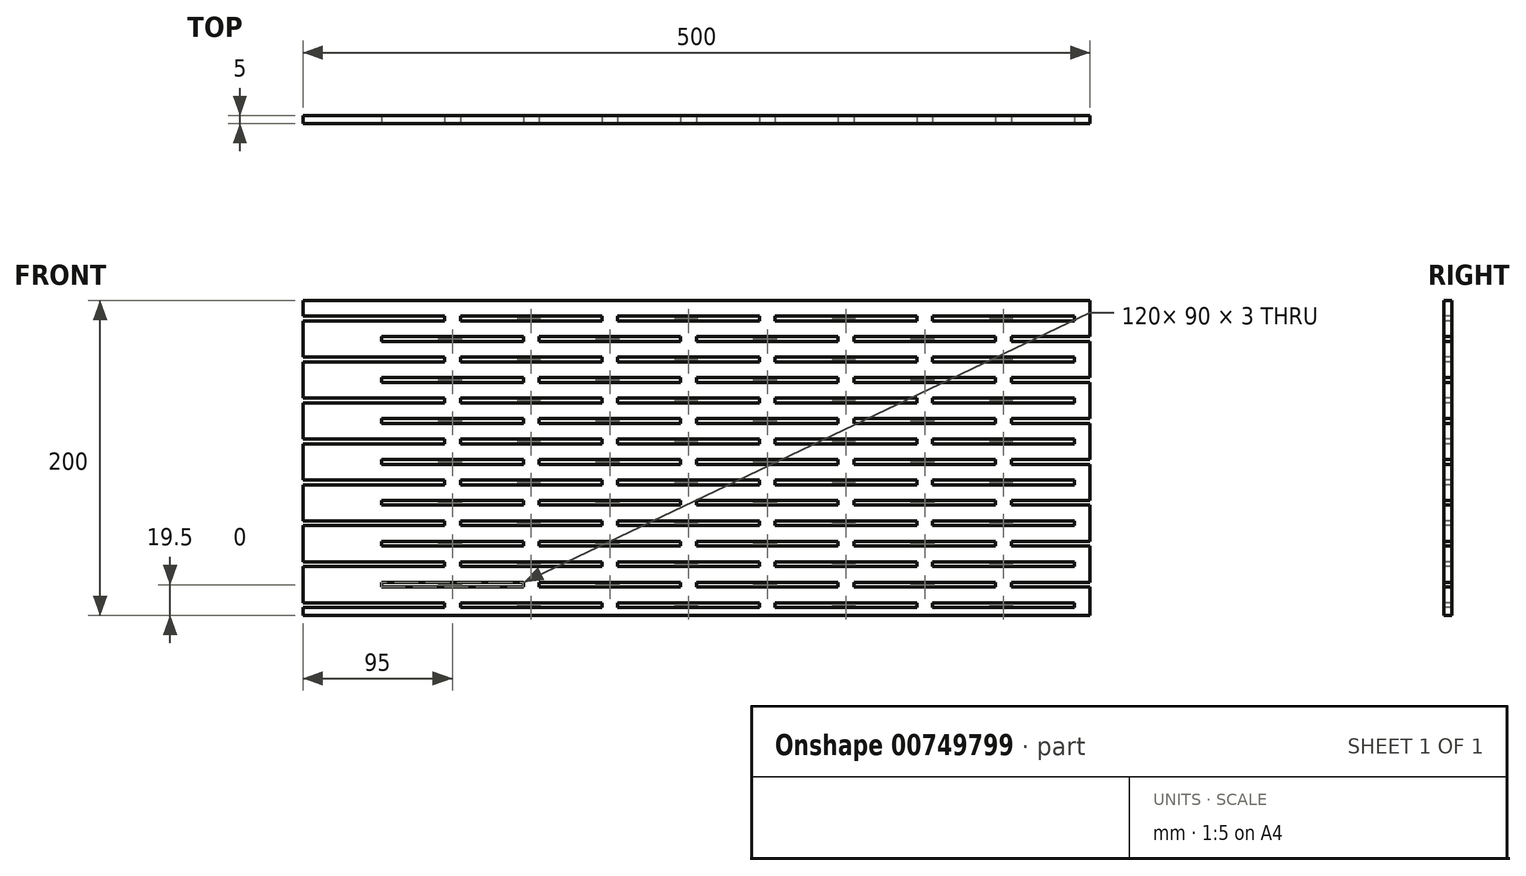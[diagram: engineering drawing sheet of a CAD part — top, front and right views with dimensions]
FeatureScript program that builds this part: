
annotation { "Feature Type Name" : "Feature", "Feature Type Description" : "" }
export const myFeature = defineFeature(function(context is Context, id is Id, definition is map)
    precondition{}
    {
        {
            var Q0;
            Q0=qCreatedBy(makeId("Front.planeOp"),FACE);
            var sketch = newSketch(context, id + "F0", { "sketchPlane" : qUnion([Q0])});
            skLineSegment(sketch, "E0.bottom", {"start": v(-250, 100) * mm, "end": v(250, 100) * mm});
            skLineSegment(sketch, "E0.top", {"start": v(-250, -100) * mm, "end": v(250, -100) * mm});
            skLineSegment(sketch, "E0.left", {"start": v(-250, 100) * mm, "end": v(-250, -100) * mm});
            skLineSegment(sketch, "E0.right", {"start": v(250, 100) * mm, "end": v(250, -100) * mm});
            skPoint(sketch, "E0.middle", {"position": v(0, 0) * mm});
            skSolve(sketch);
        }
        {
            var Q0;
            Q0=makeQuery(id+"F0.imprint","IMPRINT",FACE,{"disambiguationData":[TD([[makeQuery(id+"F0.imprint","IMPRINT",EDGE,{"derivedFrom":sQuery(id+"F0.wireOp",EDGE,"E0.bottom")}),-1.0]])]});
            extrude(context, id + "F1", {"entities" : qUnion([Q0]), "depth" : 5 * mm, "offsetDistance" : 25 * mm});
        }
        {
            var Q0;
            Q0=makeQuery(id+"F1.opExtrude","CAP_FACE",FACE,{"disambiguationData":[OSD([sQuery(id+"F0.wireOp",EDGE,"E0.bottom"),sQuery(id+"F0.wireOp",EDGE,"E0.top"),sQuery(id+"F0.wireOp",EDGE,"E0.left"),sQuery(id+"F0.wireOp",EDGE,"E0.right")])],"isStart":false});
            var sketch = newSketch(context, id + "F2", { "sketchPlane" : qUnion([Q0])});
            skLineSegment(sketch, "E1.bottom", {"start": v(-250, 90) * mm, "end": v(-160, 90) * mm});
            skLineSegment(sketch, "E1.top", {"start": v(-250, 87) * mm, "end": v(-160, 87) * mm});
            skLineSegment(sketch, "E1.left", {"start": v(-250, 90) * mm, "end": v(-250, 87) * mm});
            skLineSegment(sketch, "E1.right", {"start": v(-160, 90) * mm, "end": v(-160, 87) * mm});
            skLineSegment(sketch, "E2.bottom", {"start": v(-200, 77) * mm, "end": v(-110, 77) * mm});
            skLineSegment(sketch, "E2.top", {"start": v(-200, 74) * mm, "end": v(-110, 74) * mm});
            skLineSegment(sketch, "E2.left", {"start": v(-200, 77) * mm, "end": v(-200, 74) * mm});
            skLineSegment(sketch, "E2.right", {"start": v(-110, 77) * mm, "end": v(-110, 74) * mm});
            skLineSegment(sketch, "E3.0.1.0", {"start": v(-250, 64) * mm, "end": v(-160, 64) * mm});
            skLineSegment(sketch, "E3.0.1.1", {"start": v(-200, 51) * mm, "end": v(-110, 51) * mm});
            skLineSegment(sketch, "E3.0.1.2", {"start": v(-200, 48) * mm, "end": v(-110, 48) * mm});
            skLineSegment(sketch, "E3.0.1.3", {"start": v(-250, 61) * mm, "end": v(-160, 61) * mm});
            skLineSegment(sketch, "E3.0.1.4", {"start": v(-110, 51) * mm, "end": v(-110, 48) * mm});
            skLineSegment(sketch, "E3.0.1.5", {"start": v(-160, 64) * mm, "end": v(-160, 61) * mm});
            skLineSegment(sketch, "E3.0.1.6", {"start": v(-250, 64) * mm, "end": v(-250, 61) * mm});
            skLineSegment(sketch, "E3.0.1.7", {"start": v(-200, 51) * mm, "end": v(-200, 48) * mm});
            skLineSegment(sketch, "E3.0.2.0", {"start": v(-250, 38) * mm, "end": v(-160, 38) * mm});
            skLineSegment(sketch, "E3.0.2.1", {"start": v(-200, 25) * mm, "end": v(-110, 25) * mm});
            skLineSegment(sketch, "E3.0.2.2", {"start": v(-200, 22) * mm, "end": v(-110, 22) * mm});
            skLineSegment(sketch, "E3.0.2.3", {"start": v(-250, 35) * mm, "end": v(-160, 35) * mm});
            skLineSegment(sketch, "E3.0.2.4", {"start": v(-110, 25) * mm, "end": v(-110, 22) * mm});
            skLineSegment(sketch, "E3.0.2.5", {"start": v(-160, 38) * mm, "end": v(-160, 35) * mm});
            skLineSegment(sketch, "E3.0.2.6", {"start": v(-250, 38) * mm, "end": v(-250, 35) * mm});
            skLineSegment(sketch, "E3.0.2.7", {"start": v(-200, 25) * mm, "end": v(-200, 22) * mm});
            skLineSegment(sketch, "E3.0.3.0", {"start": v(-250, 12) * mm, "end": v(-160, 12) * mm});
            skLineSegment(sketch, "E3.0.3.1", {"start": v(-200, -1) * mm, "end": v(-110, -1) * mm});
            skLineSegment(sketch, "E3.0.3.2", {"start": v(-200, -4) * mm, "end": v(-110, -4) * mm});
            skLineSegment(sketch, "E3.0.3.3", {"start": v(-250, 9) * mm, "end": v(-160, 9) * mm});
            skLineSegment(sketch, "E3.0.3.4", {"start": v(-110, -1) * mm, "end": v(-110, -4) * mm});
            skLineSegment(sketch, "E3.0.3.5", {"start": v(-160, 12) * mm, "end": v(-160, 9) * mm});
            skLineSegment(sketch, "E3.0.3.6", {"start": v(-250, 12) * mm, "end": v(-250, 9) * mm});
            skLineSegment(sketch, "E3.0.3.7", {"start": v(-200, -1) * mm, "end": v(-200, -4) * mm});
            skLineSegment(sketch, "E3.0.4.0", {"start": v(-250, -14) * mm, "end": v(-160, -14) * mm});
            skLineSegment(sketch, "E3.0.4.1", {"start": v(-200, -27) * mm, "end": v(-110, -27) * mm});
            skLineSegment(sketch, "E3.0.4.2", {"start": v(-200, -30) * mm, "end": v(-110, -30) * mm});
            skLineSegment(sketch, "E3.0.4.3", {"start": v(-250, -17) * mm, "end": v(-160, -17) * mm});
            skLineSegment(sketch, "E3.0.4.4", {"start": v(-110, -27) * mm, "end": v(-110, -30) * mm});
            skLineSegment(sketch, "E3.0.4.5", {"start": v(-160, -14) * mm, "end": v(-160, -17) * mm});
            skLineSegment(sketch, "E3.0.4.6", {"start": v(-250, -14) * mm, "end": v(-250, -17) * mm});
            skLineSegment(sketch, "E3.0.4.7", {"start": v(-200, -27) * mm, "end": v(-200, -30) * mm});
            skLineSegment(sketch, "E3.0.5.0", {"start": v(-250, -40) * mm, "end": v(-160, -40) * mm});
            skLineSegment(sketch, "E3.0.5.1", {"start": v(-200, -53) * mm, "end": v(-110, -53) * mm});
            skLineSegment(sketch, "E3.0.5.2", {"start": v(-200, -56) * mm, "end": v(-110, -56) * mm});
            skLineSegment(sketch, "E3.0.5.3", {"start": v(-250, -43) * mm, "end": v(-160, -43) * mm});
            skLineSegment(sketch, "E3.0.5.4", {"start": v(-110, -53) * mm, "end": v(-110, -56) * mm});
            skLineSegment(sketch, "E3.0.5.5", {"start": v(-160, -40) * mm, "end": v(-160, -43) * mm});
            skLineSegment(sketch, "E3.0.5.6", {"start": v(-250, -40) * mm, "end": v(-250, -43) * mm});
            skLineSegment(sketch, "E3.0.5.7", {"start": v(-200, -53) * mm, "end": v(-200, -56) * mm});
            skLineSegment(sketch, "E3.0.6.0", {"start": v(-250, -66) * mm, "end": v(-160, -66) * mm});
            skLineSegment(sketch, "E3.0.6.1", {"start": v(-200, -79) * mm, "end": v(-110, -79) * mm});
            skLineSegment(sketch, "E3.0.6.2", {"start": v(-200, -82) * mm, "end": v(-110, -82) * mm});
            skLineSegment(sketch, "E3.0.6.3", {"start": v(-250, -69) * mm, "end": v(-160, -69) * mm});
            skLineSegment(sketch, "E3.0.6.4", {"start": v(-110, -79) * mm, "end": v(-110, -82) * mm});
            skLineSegment(sketch, "E3.0.6.5", {"start": v(-160, -66) * mm, "end": v(-160, -69) * mm});
            skLineSegment(sketch, "E3.0.6.6", {"start": v(-250, -66) * mm, "end": v(-250, -69) * mm});
            skLineSegment(sketch, "E3.0.6.7", {"start": v(-200, -79) * mm, "end": v(-200, -82) * mm});
            skLineSegment(sketch, "E3.0.7.0", {"start": v(-250, -92) * mm, "end": v(-160, -92) * mm});
            skLineSegment(sketch, "E3.0.7.1", {"start": v(-200, -105) * mm, "end": v(-110, -105) * mm});
            skLineSegment(sketch, "E3.0.7.2", {"start": v(-200, -108) * mm, "end": v(-110, -108) * mm});
            skLineSegment(sketch, "E3.0.7.3", {"start": v(-250, -95) * mm, "end": v(-160, -95) * mm});
            skLineSegment(sketch, "E3.0.7.4", {"start": v(-110, -105) * mm, "end": v(-110, -108) * mm});
            skLineSegment(sketch, "E3.0.7.5", {"start": v(-160, -92) * mm, "end": v(-160, -95) * mm});
            skLineSegment(sketch, "E3.0.7.6", {"start": v(-250, -92) * mm, "end": v(-250, -95) * mm});
            skLineSegment(sketch, "E3.0.7.7", {"start": v(-200, -105) * mm, "end": v(-200, -108) * mm});
            skLineSegment(sketch, "E3.1.0.0", {"start": v(-150, 90) * mm, "end": v(-60, 90) * mm});
            skLineSegment(sketch, "E3.1.0.1", {"start": v(-100, 77) * mm, "end": v(-10, 77) * mm});
            skLineSegment(sketch, "E3.1.0.2", {"start": v(-100, 74) * mm, "end": v(-10, 74) * mm});
            skLineSegment(sketch, "E3.1.0.3", {"start": v(-150, 87) * mm, "end": v(-60, 87) * mm});
            skLineSegment(sketch, "E3.1.0.4", {"start": v(-10, 77) * mm, "end": v(-10, 74) * mm});
            skLineSegment(sketch, "E3.1.0.5", {"start": v(-60, 90) * mm, "end": v(-60, 87) * mm});
            skLineSegment(sketch, "E3.1.0.6", {"start": v(-150, 90) * mm, "end": v(-150, 87) * mm});
            skLineSegment(sketch, "E3.1.0.7", {"start": v(-100, 77) * mm, "end": v(-100, 74) * mm});
            skLineSegment(sketch, "E3.1.1.0", {"start": v(-150, 64) * mm, "end": v(-60, 64) * mm});
            skLineSegment(sketch, "E3.1.1.1", {"start": v(-100, 51) * mm, "end": v(-10, 51) * mm});
            skLineSegment(sketch, "E3.1.1.2", {"start": v(-100, 48) * mm, "end": v(-10, 48) * mm});
            skLineSegment(sketch, "E3.1.1.3", {"start": v(-150, 61) * mm, "end": v(-60, 61) * mm});
            skLineSegment(sketch, "E3.1.1.4", {"start": v(-10, 51) * mm, "end": v(-10, 48) * mm});
            skLineSegment(sketch, "E3.1.1.5", {"start": v(-60, 64) * mm, "end": v(-60, 61) * mm});
            skLineSegment(sketch, "E3.1.1.6", {"start": v(-150, 64) * mm, "end": v(-150, 61) * mm});
            skLineSegment(sketch, "E3.1.1.7", {"start": v(-100, 51) * mm, "end": v(-100, 48) * mm});
            skLineSegment(sketch, "E3.1.2.0", {"start": v(-150, 38) * mm, "end": v(-60, 38) * mm});
            skLineSegment(sketch, "E3.1.2.1", {"start": v(-100, 25) * mm, "end": v(-10, 25) * mm});
            skLineSegment(sketch, "E3.1.2.2", {"start": v(-100, 22) * mm, "end": v(-10, 22) * mm});
            skLineSegment(sketch, "E3.1.2.3", {"start": v(-150, 35) * mm, "end": v(-60, 35) * mm});
            skLineSegment(sketch, "E3.1.2.4", {"start": v(-10, 25) * mm, "end": v(-10, 22) * mm});
            skLineSegment(sketch, "E3.1.2.5", {"start": v(-60, 38) * mm, "end": v(-60, 35) * mm});
            skLineSegment(sketch, "E3.1.2.6", {"start": v(-150, 38) * mm, "end": v(-150, 35) * mm});
            skLineSegment(sketch, "E3.1.2.7", {"start": v(-100, 25) * mm, "end": v(-100, 22) * mm});
            skLineSegment(sketch, "E3.1.3.0", {"start": v(-150, 12) * mm, "end": v(-60, 12) * mm});
            skLineSegment(sketch, "E3.1.3.1", {"start": v(-100, -1) * mm, "end": v(-10, -1) * mm});
            skLineSegment(sketch, "E3.1.3.2", {"start": v(-100, -4) * mm, "end": v(-10, -4) * mm});
            skLineSegment(sketch, "E3.1.3.3", {"start": v(-150, 9) * mm, "end": v(-60, 9) * mm});
            skLineSegment(sketch, "E3.1.3.4", {"start": v(-10, -1) * mm, "end": v(-10, -4) * mm});
            skLineSegment(sketch, "E3.1.3.5", {"start": v(-60, 12) * mm, "end": v(-60, 9) * mm});
            skLineSegment(sketch, "E3.1.3.6", {"start": v(-150, 12) * mm, "end": v(-150, 9) * mm});
            skLineSegment(sketch, "E3.1.3.7", {"start": v(-100, -1) * mm, "end": v(-100, -4) * mm});
            skLineSegment(sketch, "E3.1.4.0", {"start": v(-150, -14) * mm, "end": v(-60, -14) * mm});
            skLineSegment(sketch, "E3.1.4.1", {"start": v(-100, -27) * mm, "end": v(-10, -27) * mm});
            skLineSegment(sketch, "E3.1.4.2", {"start": v(-100, -30) * mm, "end": v(-10, -30) * mm});
            skLineSegment(sketch, "E3.1.4.3", {"start": v(-150, -17) * mm, "end": v(-60, -17) * mm});
            skLineSegment(sketch, "E3.1.4.4", {"start": v(-10, -27) * mm, "end": v(-10, -30) * mm});
            skLineSegment(sketch, "E3.1.4.5", {"start": v(-60, -14) * mm, "end": v(-60, -17) * mm});
            skLineSegment(sketch, "E3.1.4.6", {"start": v(-150, -14) * mm, "end": v(-150, -17) * mm});
            skLineSegment(sketch, "E3.1.4.7", {"start": v(-100, -27) * mm, "end": v(-100, -30) * mm});
            skLineSegment(sketch, "E3.1.5.0", {"start": v(-150, -40) * mm, "end": v(-60, -40) * mm});
            skLineSegment(sketch, "E3.1.5.1", {"start": v(-100, -53) * mm, "end": v(-10, -53) * mm});
            skLineSegment(sketch, "E3.1.5.2", {"start": v(-100, -56) * mm, "end": v(-10, -56) * mm});
            skLineSegment(sketch, "E3.1.5.3", {"start": v(-150, -43) * mm, "end": v(-60, -43) * mm});
            skLineSegment(sketch, "E3.1.5.4", {"start": v(-10, -53) * mm, "end": v(-10, -56) * mm});
            skLineSegment(sketch, "E3.1.5.5", {"start": v(-60, -40) * mm, "end": v(-60, -43) * mm});
            skLineSegment(sketch, "E3.1.5.6", {"start": v(-150, -40) * mm, "end": v(-150, -43) * mm});
            skLineSegment(sketch, "E3.1.5.7", {"start": v(-100, -53) * mm, "end": v(-100, -56) * mm});
            skLineSegment(sketch, "E3.1.6.0", {"start": v(-150, -66) * mm, "end": v(-60, -66) * mm});
            skLineSegment(sketch, "E3.1.6.1", {"start": v(-100, -79) * mm, "end": v(-10, -79) * mm});
            skLineSegment(sketch, "E3.1.6.2", {"start": v(-100, -82) * mm, "end": v(-10, -82) * mm});
            skLineSegment(sketch, "E3.1.6.3", {"start": v(-150, -69) * mm, "end": v(-60, -69) * mm});
            skLineSegment(sketch, "E3.1.6.4", {"start": v(-10, -79) * mm, "end": v(-10, -82) * mm});
            skLineSegment(sketch, "E3.1.6.5", {"start": v(-60, -66) * mm, "end": v(-60, -69) * mm});
            skLineSegment(sketch, "E3.1.6.6", {"start": v(-150, -66) * mm, "end": v(-150, -69) * mm});
            skLineSegment(sketch, "E3.1.6.7", {"start": v(-100, -79) * mm, "end": v(-100, -82) * mm});
            skLineSegment(sketch, "E3.1.7.0", {"start": v(-150, -92) * mm, "end": v(-60, -92) * mm});
            skLineSegment(sketch, "E3.1.7.1", {"start": v(-100, -105) * mm, "end": v(-10, -105) * mm});
            skLineSegment(sketch, "E3.1.7.2", {"start": v(-100, -108) * mm, "end": v(-10, -108) * mm});
            skLineSegment(sketch, "E3.1.7.3", {"start": v(-150, -95) * mm, "end": v(-60, -95) * mm});
            skLineSegment(sketch, "E3.1.7.4", {"start": v(-10, -105) * mm, "end": v(-10, -108) * mm});
            skLineSegment(sketch, "E3.1.7.5", {"start": v(-60, -92) * mm, "end": v(-60, -95) * mm});
            skLineSegment(sketch, "E3.1.7.6", {"start": v(-150, -92) * mm, "end": v(-150, -95) * mm});
            skLineSegment(sketch, "E3.1.7.7", {"start": v(-100, -105) * mm, "end": v(-100, -108) * mm});
            skLineSegment(sketch, "E3.2.0.0", {"start": v(-50, 90) * mm, "end": v(40, 90) * mm});
            skLineSegment(sketch, "E3.2.0.1", {"start": v(0, 77) * mm, "end": v(90, 77) * mm});
            skLineSegment(sketch, "E3.2.0.2", {"start": v(0, 74) * mm, "end": v(90, 74) * mm});
            skLineSegment(sketch, "E3.2.0.3", {"start": v(-50, 87) * mm, "end": v(40, 87) * mm});
            skLineSegment(sketch, "E3.2.0.4", {"start": v(90, 77) * mm, "end": v(90, 74) * mm});
            skLineSegment(sketch, "E3.2.0.5", {"start": v(40, 90) * mm, "end": v(40, 87) * mm});
            skLineSegment(sketch, "E3.2.0.6", {"start": v(-50, 90) * mm, "end": v(-50, 87) * mm});
            skLineSegment(sketch, "E3.2.0.7", {"start": v(0, 77) * mm, "end": v(0, 74) * mm});
            skLineSegment(sketch, "E3.2.1.0", {"start": v(-50, 64) * mm, "end": v(40, 64) * mm});
            skLineSegment(sketch, "E3.2.1.1", {"start": v(0, 51) * mm, "end": v(90, 51) * mm});
            skLineSegment(sketch, "E3.2.1.2", {"start": v(0, 48) * mm, "end": v(90, 48) * mm});
            skLineSegment(sketch, "E3.2.1.3", {"start": v(-50, 61) * mm, "end": v(40, 61) * mm});
            skLineSegment(sketch, "E3.2.1.4", {"start": v(90, 51) * mm, "end": v(90, 48) * mm});
            skLineSegment(sketch, "E3.2.1.5", {"start": v(40, 64) * mm, "end": v(40, 61) * mm});
            skLineSegment(sketch, "E3.2.1.6", {"start": v(-50, 64) * mm, "end": v(-50, 61) * mm});
            skLineSegment(sketch, "E3.2.1.7", {"start": v(0, 51) * mm, "end": v(0, 48) * mm});
            skLineSegment(sketch, "E3.2.2.0", {"start": v(-50, 38) * mm, "end": v(40, 38) * mm});
            skLineSegment(sketch, "E3.2.2.1", {"start": v(0, 25) * mm, "end": v(90, 25) * mm});
            skLineSegment(sketch, "E3.2.2.2", {"start": v(0, 22) * mm, "end": v(90, 22) * mm});
            skLineSegment(sketch, "E3.2.2.3", {"start": v(-50, 35) * mm, "end": v(40, 35) * mm});
            skLineSegment(sketch, "E3.2.2.4", {"start": v(90, 25) * mm, "end": v(90, 22) * mm});
            skLineSegment(sketch, "E3.2.2.5", {"start": v(40, 38) * mm, "end": v(40, 35) * mm});
            skLineSegment(sketch, "E3.2.2.6", {"start": v(-50, 38) * mm, "end": v(-50, 35) * mm});
            skLineSegment(sketch, "E3.2.2.7", {"start": v(0, 25) * mm, "end": v(0, 22) * mm});
            skLineSegment(sketch, "E3.2.3.0", {"start": v(-50, 12) * mm, "end": v(40, 12) * mm});
            skLineSegment(sketch, "E3.2.3.1", {"start": v(0, -1) * mm, "end": v(90, -1) * mm});
            skLineSegment(sketch, "E3.2.3.2", {"start": v(0, -4) * mm, "end": v(90, -4) * mm});
            skLineSegment(sketch, "E3.2.3.3", {"start": v(-50, 9) * mm, "end": v(40, 9) * mm});
            skLineSegment(sketch, "E3.2.3.4", {"start": v(90, -1) * mm, "end": v(90, -4) * mm});
            skLineSegment(sketch, "E3.2.3.5", {"start": v(40, 12) * mm, "end": v(40, 9) * mm});
            skLineSegment(sketch, "E3.2.3.6", {"start": v(-50, 12) * mm, "end": v(-50, 9) * mm});
            skLineSegment(sketch, "E3.2.3.7", {"start": v(0, -1) * mm, "end": v(0, -4) * mm});
            skLineSegment(sketch, "E3.2.4.0", {"start": v(-50, -14) * mm, "end": v(40, -14) * mm});
            skLineSegment(sketch, "E3.2.4.1", {"start": v(0, -27) * mm, "end": v(90, -27) * mm});
            skLineSegment(sketch, "E3.2.4.2", {"start": v(0, -30) * mm, "end": v(90, -30) * mm});
            skLineSegment(sketch, "E3.2.4.3", {"start": v(-50, -17) * mm, "end": v(40, -17) * mm});
            skLineSegment(sketch, "E3.2.4.4", {"start": v(90, -27) * mm, "end": v(90, -30) * mm});
            skLineSegment(sketch, "E3.2.4.5", {"start": v(40, -14) * mm, "end": v(40, -17) * mm});
            skLineSegment(sketch, "E3.2.4.6", {"start": v(-50, -14) * mm, "end": v(-50, -17) * mm});
            skLineSegment(sketch, "E3.2.4.7", {"start": v(0, -27) * mm, "end": v(0, -30) * mm});
            skLineSegment(sketch, "E3.2.5.0", {"start": v(-50, -40) * mm, "end": v(40, -40) * mm});
            skLineSegment(sketch, "E3.2.5.1", {"start": v(0, -53) * mm, "end": v(90, -53) * mm});
            skLineSegment(sketch, "E3.2.5.2", {"start": v(0, -56) * mm, "end": v(90, -56) * mm});
            skLineSegment(sketch, "E3.2.5.3", {"start": v(-50, -43) * mm, "end": v(40, -43) * mm});
            skLineSegment(sketch, "E3.2.5.4", {"start": v(90, -53) * mm, "end": v(90, -56) * mm});
            skLineSegment(sketch, "E3.2.5.5", {"start": v(40, -40) * mm, "end": v(40, -43) * mm});
            skLineSegment(sketch, "E3.2.5.6", {"start": v(-50, -40) * mm, "end": v(-50, -43) * mm});
            skLineSegment(sketch, "E3.2.5.7", {"start": v(0, -53) * mm, "end": v(0, -56) * mm});
            skLineSegment(sketch, "E3.2.6.0", {"start": v(-50, -66) * mm, "end": v(40, -66) * mm});
            skLineSegment(sketch, "E3.2.6.1", {"start": v(0, -79) * mm, "end": v(90, -79) * mm});
            skLineSegment(sketch, "E3.2.6.2", {"start": v(0, -82) * mm, "end": v(90, -82) * mm});
            skLineSegment(sketch, "E3.2.6.3", {"start": v(-50, -69) * mm, "end": v(40, -69) * mm});
            skLineSegment(sketch, "E3.2.6.4", {"start": v(90, -79) * mm, "end": v(90, -82) * mm});
            skLineSegment(sketch, "E3.2.6.5", {"start": v(40, -66) * mm, "end": v(40, -69) * mm});
            skLineSegment(sketch, "E3.2.6.6", {"start": v(-50, -66) * mm, "end": v(-50, -69) * mm});
            skLineSegment(sketch, "E3.2.6.7", {"start": v(0, -79) * mm, "end": v(0, -82) * mm});
            skLineSegment(sketch, "E3.2.7.0", {"start": v(-50, -92) * mm, "end": v(40, -92) * mm});
            skLineSegment(sketch, "E3.2.7.1", {"start": v(0, -105) * mm, "end": v(90, -105) * mm});
            skLineSegment(sketch, "E3.2.7.2", {"start": v(0, -108) * mm, "end": v(90, -108) * mm});
            skLineSegment(sketch, "E3.2.7.3", {"start": v(-50, -95) * mm, "end": v(40, -95) * mm});
            skLineSegment(sketch, "E3.2.7.4", {"start": v(90, -105) * mm, "end": v(90, -108) * mm});
            skLineSegment(sketch, "E3.2.7.5", {"start": v(40, -92) * mm, "end": v(40, -95) * mm});
            skLineSegment(sketch, "E3.2.7.6", {"start": v(-50, -92) * mm, "end": v(-50, -95) * mm});
            skLineSegment(sketch, "E3.2.7.7", {"start": v(0, -105) * mm, "end": v(0, -108) * mm});
            skLineSegment(sketch, "E3.3.0.0", {"start": v(50, 90) * mm, "end": v(140, 90) * mm});
            skLineSegment(sketch, "E3.3.0.1", {"start": v(100, 77) * mm, "end": v(190, 77) * mm});
            skLineSegment(sketch, "E3.3.0.2", {"start": v(100, 74) * mm, "end": v(190, 74) * mm});
            skLineSegment(sketch, "E3.3.0.3", {"start": v(50, 87) * mm, "end": v(140, 87) * mm});
            skLineSegment(sketch, "E3.3.0.4", {"start": v(190, 77) * mm, "end": v(190, 74) * mm});
            skLineSegment(sketch, "E3.3.0.5", {"start": v(140, 90) * mm, "end": v(140, 87) * mm});
            skLineSegment(sketch, "E3.3.0.6", {"start": v(50, 90) * mm, "end": v(50, 87) * mm});
            skLineSegment(sketch, "E3.3.0.7", {"start": v(100, 77) * mm, "end": v(100, 74) * mm});
            skLineSegment(sketch, "E3.3.1.0", {"start": v(50, 64) * mm, "end": v(140, 64) * mm});
            skLineSegment(sketch, "E3.3.1.1", {"start": v(100, 51) * mm, "end": v(190, 51) * mm});
            skLineSegment(sketch, "E3.3.1.2", {"start": v(100, 48) * mm, "end": v(190, 48) * mm});
            skLineSegment(sketch, "E3.3.1.3", {"start": v(50, 61) * mm, "end": v(140, 61) * mm});
            skLineSegment(sketch, "E3.3.1.4", {"start": v(190, 51) * mm, "end": v(190, 48) * mm});
            skLineSegment(sketch, "E3.3.1.5", {"start": v(140, 64) * mm, "end": v(140, 61) * mm});
            skLineSegment(sketch, "E3.3.1.6", {"start": v(50, 64) * mm, "end": v(50, 61) * mm});
            skLineSegment(sketch, "E3.3.1.7", {"start": v(100, 51) * mm, "end": v(100, 48) * mm});
            skLineSegment(sketch, "E3.3.2.0", {"start": v(50, 38) * mm, "end": v(140, 38) * mm});
            skLineSegment(sketch, "E3.3.2.1", {"start": v(100, 25) * mm, "end": v(190, 25) * mm});
            skLineSegment(sketch, "E3.3.2.2", {"start": v(100, 22) * mm, "end": v(190, 22) * mm});
            skLineSegment(sketch, "E3.3.2.3", {"start": v(50, 35) * mm, "end": v(140, 35) * mm});
            skLineSegment(sketch, "E3.3.2.4", {"start": v(190, 25) * mm, "end": v(190, 22) * mm});
            skLineSegment(sketch, "E3.3.2.5", {"start": v(140, 38) * mm, "end": v(140, 35) * mm});
            skLineSegment(sketch, "E3.3.2.6", {"start": v(50, 38) * mm, "end": v(50, 35) * mm});
            skLineSegment(sketch, "E3.3.2.7", {"start": v(100, 25) * mm, "end": v(100, 22) * mm});
            skLineSegment(sketch, "E3.3.3.0", {"start": v(50, 12) * mm, "end": v(140, 12) * mm});
            skLineSegment(sketch, "E3.3.3.1", {"start": v(100, -1) * mm, "end": v(190, -1) * mm});
            skLineSegment(sketch, "E3.3.3.2", {"start": v(100, -4) * mm, "end": v(190, -4) * mm});
            skLineSegment(sketch, "E3.3.3.3", {"start": v(50, 9) * mm, "end": v(140, 9) * mm});
            skLineSegment(sketch, "E3.3.3.4", {"start": v(190, -1) * mm, "end": v(190, -4) * mm});
            skLineSegment(sketch, "E3.3.3.5", {"start": v(140, 12) * mm, "end": v(140, 9) * mm});
            skLineSegment(sketch, "E3.3.3.6", {"start": v(50, 12) * mm, "end": v(50, 9) * mm});
            skLineSegment(sketch, "E3.3.3.7", {"start": v(100, -1) * mm, "end": v(100, -4) * mm});
            skLineSegment(sketch, "E3.3.4.0", {"start": v(50, -14) * mm, "end": v(140, -14) * mm});
            skLineSegment(sketch, "E3.3.4.1", {"start": v(100, -27) * mm, "end": v(190, -27) * mm});
            skLineSegment(sketch, "E3.3.4.2", {"start": v(100, -30) * mm, "end": v(190, -30) * mm});
            skLineSegment(sketch, "E3.3.4.3", {"start": v(50, -17) * mm, "end": v(140, -17) * mm});
            skLineSegment(sketch, "E3.3.4.4", {"start": v(190, -27) * mm, "end": v(190, -30) * mm});
            skLineSegment(sketch, "E3.3.4.5", {"start": v(140, -14) * mm, "end": v(140, -17) * mm});
            skLineSegment(sketch, "E3.3.4.6", {"start": v(50, -14) * mm, "end": v(50, -17) * mm});
            skLineSegment(sketch, "E3.3.4.7", {"start": v(100, -27) * mm, "end": v(100, -30) * mm});
            skLineSegment(sketch, "E3.3.5.0", {"start": v(50, -40) * mm, "end": v(140, -40) * mm});
            skLineSegment(sketch, "E3.3.5.1", {"start": v(100, -53) * mm, "end": v(190, -53) * mm});
            skLineSegment(sketch, "E3.3.5.2", {"start": v(100, -56) * mm, "end": v(190, -56) * mm});
            skLineSegment(sketch, "E3.3.5.3", {"start": v(50, -43) * mm, "end": v(140, -43) * mm});
            skLineSegment(sketch, "E3.3.5.4", {"start": v(190, -53) * mm, "end": v(190, -56) * mm});
            skLineSegment(sketch, "E3.3.5.5", {"start": v(140, -40) * mm, "end": v(140, -43) * mm});
            skLineSegment(sketch, "E3.3.5.6", {"start": v(50, -40) * mm, "end": v(50, -43) * mm});
            skLineSegment(sketch, "E3.3.5.7", {"start": v(100, -53) * mm, "end": v(100, -56) * mm});
            skLineSegment(sketch, "E3.3.6.0", {"start": v(50, -66) * mm, "end": v(140, -66) * mm});
            skLineSegment(sketch, "E3.3.6.1", {"start": v(100, -79) * mm, "end": v(190, -79) * mm});
            skLineSegment(sketch, "E3.3.6.2", {"start": v(100, -82) * mm, "end": v(190, -82) * mm});
            skLineSegment(sketch, "E3.3.6.3", {"start": v(50, -69) * mm, "end": v(140, -69) * mm});
            skLineSegment(sketch, "E3.3.6.4", {"start": v(190, -79) * mm, "end": v(190, -82) * mm});
            skLineSegment(sketch, "E3.3.6.5", {"start": v(140, -66) * mm, "end": v(140, -69) * mm});
            skLineSegment(sketch, "E3.3.6.6", {"start": v(50, -66) * mm, "end": v(50, -69) * mm});
            skLineSegment(sketch, "E3.3.6.7", {"start": v(100, -79) * mm, "end": v(100, -82) * mm});
            skLineSegment(sketch, "E3.3.7.0", {"start": v(50, -92) * mm, "end": v(140, -92) * mm});
            skLineSegment(sketch, "E3.3.7.1", {"start": v(100, -105) * mm, "end": v(190, -105) * mm});
            skLineSegment(sketch, "E3.3.7.2", {"start": v(100, -108) * mm, "end": v(190, -108) * mm});
            skLineSegment(sketch, "E3.3.7.3", {"start": v(50, -95) * mm, "end": v(140, -95) * mm});
            skLineSegment(sketch, "E3.3.7.4", {"start": v(190, -105) * mm, "end": v(190, -108) * mm});
            skLineSegment(sketch, "E3.3.7.5", {"start": v(140, -92) * mm, "end": v(140, -95) * mm});
            skLineSegment(sketch, "E3.3.7.6", {"start": v(50, -92) * mm, "end": v(50, -95) * mm});
            skLineSegment(sketch, "E3.3.7.7", {"start": v(100, -105) * mm, "end": v(100, -108) * mm});
            skLineSegment(sketch, "E3.4.0.0", {"start": v(150, 90) * mm, "end": v(240, 90) * mm});
            skLineSegment(sketch, "E3.4.0.1", {"start": v(200, 77) * mm, "end": v(290, 77) * mm});
            skLineSegment(sketch, "E3.4.0.2", {"start": v(200, 74) * mm, "end": v(290, 74) * mm});
            skLineSegment(sketch, "E3.4.0.3", {"start": v(150, 87) * mm, "end": v(240, 87) * mm});
            skLineSegment(sketch, "E3.4.0.4", {"start": v(290, 77) * mm, "end": v(290, 74) * mm});
            skLineSegment(sketch, "E3.4.0.5", {"start": v(240, 90) * mm, "end": v(240, 87) * mm});
            skLineSegment(sketch, "E3.4.0.6", {"start": v(150, 90) * mm, "end": v(150, 87) * mm});
            skLineSegment(sketch, "E3.4.0.7", {"start": v(200, 77) * mm, "end": v(200, 74) * mm});
            skLineSegment(sketch, "E3.4.1.0", {"start": v(150, 64) * mm, "end": v(240, 64) * mm});
            skLineSegment(sketch, "E3.4.1.1", {"start": v(200, 51) * mm, "end": v(290, 51) * mm});
            skLineSegment(sketch, "E3.4.1.2", {"start": v(200, 48) * mm, "end": v(290, 48) * mm});
            skLineSegment(sketch, "E3.4.1.3", {"start": v(150, 61) * mm, "end": v(240, 61) * mm});
            skLineSegment(sketch, "E3.4.1.4", {"start": v(290, 51) * mm, "end": v(290, 48) * mm});
            skLineSegment(sketch, "E3.4.1.5", {"start": v(240, 64) * mm, "end": v(240, 61) * mm});
            skLineSegment(sketch, "E3.4.1.6", {"start": v(150, 64) * mm, "end": v(150, 61) * mm});
            skLineSegment(sketch, "E3.4.1.7", {"start": v(200, 51) * mm, "end": v(200, 48) * mm});
            skLineSegment(sketch, "E3.4.2.0", {"start": v(150, 38) * mm, "end": v(240, 38) * mm});
            skLineSegment(sketch, "E3.4.2.1", {"start": v(200, 25) * mm, "end": v(290, 25) * mm});
            skLineSegment(sketch, "E3.4.2.2", {"start": v(200, 22) * mm, "end": v(290, 22) * mm});
            skLineSegment(sketch, "E3.4.2.3", {"start": v(150, 35) * mm, "end": v(240, 35) * mm});
            skLineSegment(sketch, "E3.4.2.4", {"start": v(290, 25) * mm, "end": v(290, 22) * mm});
            skLineSegment(sketch, "E3.4.2.5", {"start": v(240, 38) * mm, "end": v(240, 35) * mm});
            skLineSegment(sketch, "E3.4.2.6", {"start": v(150, 38) * mm, "end": v(150, 35) * mm});
            skLineSegment(sketch, "E3.4.2.7", {"start": v(200, 25) * mm, "end": v(200, 22) * mm});
            skLineSegment(sketch, "E3.4.3.0", {"start": v(150, 12) * mm, "end": v(240, 12) * mm});
            skLineSegment(sketch, "E3.4.3.1", {"start": v(200, -1) * mm, "end": v(290, -1) * mm});
            skLineSegment(sketch, "E3.4.3.2", {"start": v(200, -4) * mm, "end": v(290, -4) * mm});
            skLineSegment(sketch, "E3.4.3.3", {"start": v(150, 9) * mm, "end": v(240, 9) * mm});
            skLineSegment(sketch, "E3.4.3.4", {"start": v(290, -1) * mm, "end": v(290, -4) * mm});
            skLineSegment(sketch, "E3.4.3.5", {"start": v(240, 12) * mm, "end": v(240, 9) * mm});
            skLineSegment(sketch, "E3.4.3.6", {"start": v(150, 12) * mm, "end": v(150, 9) * mm});
            skLineSegment(sketch, "E3.4.3.7", {"start": v(200, -1) * mm, "end": v(200, -4) * mm});
            skLineSegment(sketch, "E3.4.4.0", {"start": v(150, -14) * mm, "end": v(240, -14) * mm});
            skLineSegment(sketch, "E3.4.4.1", {"start": v(200, -27) * mm, "end": v(290, -27) * mm});
            skLineSegment(sketch, "E3.4.4.2", {"start": v(200, -30) * mm, "end": v(290, -30) * mm});
            skLineSegment(sketch, "E3.4.4.3", {"start": v(150, -17) * mm, "end": v(240, -17) * mm});
            skLineSegment(sketch, "E3.4.4.4", {"start": v(290, -27) * mm, "end": v(290, -30) * mm});
            skLineSegment(sketch, "E3.4.4.5", {"start": v(240, -14) * mm, "end": v(240, -17) * mm});
            skLineSegment(sketch, "E3.4.4.6", {"start": v(150, -14) * mm, "end": v(150, -17) * mm});
            skLineSegment(sketch, "E3.4.4.7", {"start": v(200, -27) * mm, "end": v(200, -30) * mm});
            skLineSegment(sketch, "E3.4.5.0", {"start": v(150, -40) * mm, "end": v(240, -40) * mm});
            skLineSegment(sketch, "E3.4.5.1", {"start": v(200, -53) * mm, "end": v(290, -53) * mm});
            skLineSegment(sketch, "E3.4.5.2", {"start": v(200, -56) * mm, "end": v(290, -56) * mm});
            skLineSegment(sketch, "E3.4.5.3", {"start": v(150, -43) * mm, "end": v(240, -43) * mm});
            skLineSegment(sketch, "E3.4.5.4", {"start": v(290, -53) * mm, "end": v(290, -56) * mm});
            skLineSegment(sketch, "E3.4.5.5", {"start": v(240, -40) * mm, "end": v(240, -43) * mm});
            skLineSegment(sketch, "E3.4.5.6", {"start": v(150, -40) * mm, "end": v(150, -43) * mm});
            skLineSegment(sketch, "E3.4.5.7", {"start": v(200, -53) * mm, "end": v(200, -56) * mm});
            skLineSegment(sketch, "E3.4.6.0", {"start": v(150, -66) * mm, "end": v(240, -66) * mm});
            skLineSegment(sketch, "E3.4.6.1", {"start": v(200, -79) * mm, "end": v(290, -79) * mm});
            skLineSegment(sketch, "E3.4.6.2", {"start": v(200, -82) * mm, "end": v(290, -82) * mm});
            skLineSegment(sketch, "E3.4.6.3", {"start": v(150, -69) * mm, "end": v(240, -69) * mm});
            skLineSegment(sketch, "E3.4.6.4", {"start": v(290, -79) * mm, "end": v(290, -82) * mm});
            skLineSegment(sketch, "E3.4.6.5", {"start": v(240, -66) * mm, "end": v(240, -69) * mm});
            skLineSegment(sketch, "E3.4.6.6", {"start": v(150, -66) * mm, "end": v(150, -69) * mm});
            skLineSegment(sketch, "E3.4.6.7", {"start": v(200, -79) * mm, "end": v(200, -82) * mm});
            skLineSegment(sketch, "E3.4.7.0", {"start": v(150, -92) * mm, "end": v(240, -92) * mm});
            skLineSegment(sketch, "E3.4.7.1", {"start": v(200, -105) * mm, "end": v(290, -105) * mm});
            skLineSegment(sketch, "E3.4.7.2", {"start": v(200, -108) * mm, "end": v(290, -108) * mm});
            skLineSegment(sketch, "E3.4.7.3", {"start": v(150, -95) * mm, "end": v(240, -95) * mm});
            skLineSegment(sketch, "E3.4.7.4", {"start": v(290, -105) * mm, "end": v(290, -108) * mm});
            skLineSegment(sketch, "E3.4.7.5", {"start": v(240, -92) * mm, "end": v(240, -95) * mm});
            skLineSegment(sketch, "E3.4.7.6", {"start": v(150, -92) * mm, "end": v(150, -95) * mm});
            skLineSegment(sketch, "E3.4.7.7", {"start": v(200, -105) * mm, "end": v(200, -108) * mm});
            skLineSegment(sketch, "E3.direction1", {"start": v(-250, 87) * mm, "end": v(-150, 87) * mm, "construction": true});
            skLineSegment(sketch, "E3.direction2", {"start": v(-250, 87) * mm, "end": v(-250, 61) * mm, "construction": true});
            skSolve(sketch);
        }
        {
            var Q0;
            Q0 = qSketchRegion(id + "F2", true);
            extrude(context, id + "F3", {"entities" : qUnion([Q0]), "operationType" : NewBodyOperationType.REMOVE, "oppositeDirection" : true, "depth" : 25 * mm, "offsetDistance" : 25 * mm});
        }
    });
